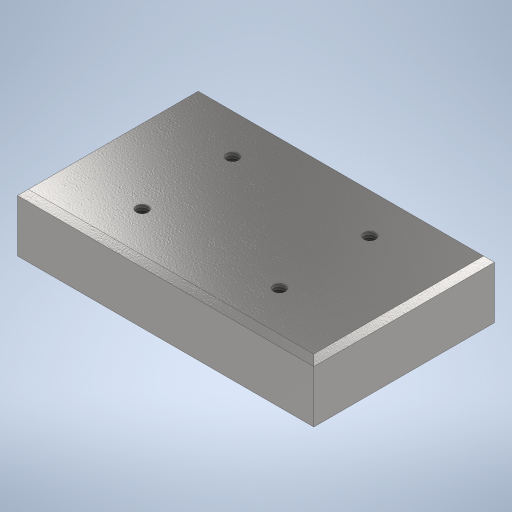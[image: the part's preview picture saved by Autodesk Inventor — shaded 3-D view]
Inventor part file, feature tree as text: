
AUTODESK INVENTOR PART (.ipt)
format: ipt  version: 2024 (Build 280153000, 153)  size: 311,808 bytes
history: native  units: mm
features: sketch x2, extrude x1, chamfer x1, hole x1
ambient origin geometry x8: Origin, YZ Plane, XZ Plane, XY Plane, X Axis, Y Axis, Z Axis, Center Point
bodies: Volumenkörper1 (feature_tree)
feature tree (5):
  extrude  "Extrusion1"  Depth=82.0mm
  chamfer  "Fasen1"  Distance=16.0mm
  hole  "Bohrung1"  [1 undecoded]
  sketch  "Skizze1"  dims[d0=50.0mm d1=82.0mm d2=16.0mm d3=0.0mm]
  sketch  "Skizze2"  dims[d4=1.5mm d5=2.0mm d6=45.0deg d7=25.0mm d8=38.0mm d9=3.242mm d10=6.0mm d11=4.0mm d12=2.0mm d13=90.0deg d14=8.0mm d15=20.594885mm]
note: 1 required parameter value undecoded (feature->parameter linkage not recoverable at this tier; creation-order binding heuristic only, values carry confidence <= 0.55)
